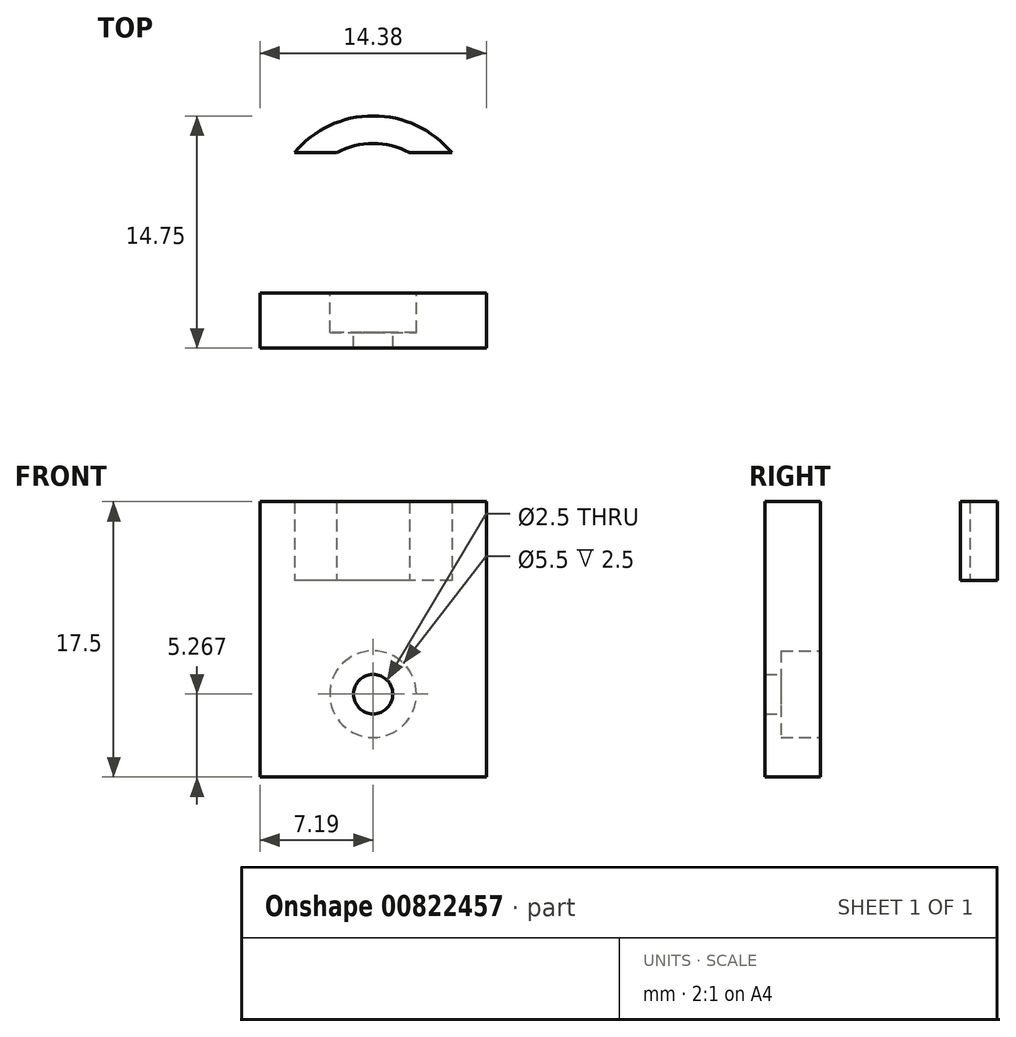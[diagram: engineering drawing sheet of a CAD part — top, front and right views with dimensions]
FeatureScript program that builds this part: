
annotation { "Feature Type Name" : "Feature", "Feature Type Description" : "" }
export const myFeature = defineFeature(function(context is Context, id is Id, definition is map)
    precondition{}
    {
        {
            var Q0;
            Q0=qCreatedBy(makeId("Top.planeOp"),FACE);
            var sketch = newSketch(context, id + "F0", { "sketchPlane" : qUnion([Q0])});
            skCircle(sketch, "E0", {"center": v(0, 0) * mm, "radius": 4.75 * mm});
            skCircle(sketch, "E1", {"center": v(0, 0) * mm, "radius": 6.5 * mm});
            skLineSegment(sketch, "E2", {"start": v(5, 4.15) * mm, "end": v(-5, 4.15) * mm});
            skLineSegment(sketch, "E3", {"start": v(0, -4.75) * mm, "end": v(-4.44, -4.75) * mm});
            skLineSegment(sketch, "E4", {"start": v(-4.44, -4.75) * mm, "end": v(-7.19, -4.75) * mm});
            skLineSegment(sketch, "E5", {"start": v(-7.19, -4.75) * mm, "end": v(-7.19, -8.25) * mm});
            skLineSegment(sketch, "E6", {"start": v(0, -4.75) * mm, "end": v(4.44, -4.75) * mm});
            skLineSegment(sketch, "E7", {"start": v(4.44, -4.75) * mm, "end": v(7.19, -4.75) * mm});
            skLineSegment(sketch, "E8", {"start": v(7.19, -4.75) * mm, "end": v(7.19, -8.25) * mm});
            skLineSegment(sketch, "E9", {"start": v(7.19, -8.25) * mm, "end": v(-7.19, -8.25) * mm});
            skSolve(sketch);
        }
        {
            var Q0;
            {var subQ0=sQuery(id+"F0.wireOp",EDGE,"E2");var subQ1=sQuery(id+"F0.wireOp",EDGE,"E0");var subQ2=makeQuery(id+"F0.imprint","INTERSECT",VERTEX,{"disambiguationData":[OD(0.0)],"derivedFrom":[subQ1,subQ0]});Q0=makeQuery(id+"F0.imprint","IMPRINT",FACE,{"disambiguationData":[TD([[makeQuery(id+"F0.imprint","IMPRINT",EDGE,{"disambiguationData":[TD([[subQ2,-1.0]])],"derivedFrom":subQ1}),-1.0]])]});}
            var Q1;
            {var subQ0=sQuery(id+"F0.wireOp",EDGE,"E2");var subQ1=sQuery(id+"F0.wireOp",EDGE,"E0");var subQ2=makeQuery(id+"F0.imprint","INTERSECT",VERTEX,{"disambiguationData":[OD(1.0)],"derivedFrom":[subQ1,subQ0]});Q1=makeQuery(id+"F0.imprint","IMPRINT",FACE,{"disambiguationData":[TD([[makeQuery(id+"F0.imprint","IMPRINT",EDGE,{"disambiguationData":[TD([[subQ2,1.0]])],"derivedFrom":subQ1}),-1.0]])]});}
            extrude(context, id + "F1", {"entities" : qUnion([Q0, Q1]), "endBound" : BoundingType.SYMMETRIC, "depth" : 5 * mm, "offsetDistance" : 25 * mm});
        }
        {
            var Q0;
            {var subQ1=sQuery(id+"F0.wireOp",EDGE,"E4");Q0=makeQuery(id+"F0.imprint","IMPRINT",FACE,{"disambiguationData":[TD([[makeQuery(id+"F0.imprint","IMPRINT",EDGE,{"derivedFrom":subQ1}),1.0]])]});}
            var Q1;
            {var subQ0=sQuery(id+"F0.wireOp",EDGE,"E3");Q1=makeQuery(id+"F0.imprint","IMPRINT",FACE,{"disambiguationData":[TD([[makeQuery(id+"F0.imprint","IMPRINT",EDGE,{"derivedFrom":subQ0}),1.0]])]});}
            extrude(context, id + "F2", {"entities" : qUnion([Q0, Q1]), "oppositeDirection" : true, "depth" : 15 * mm, "offsetDistance" : 25 * mm, "hasSecondDirection" : true, "secondDirectionOppositeDirection" : false, "secondDirectionDepth" : 2.5 * mm});
        }
        {
            var Q0;
            Q0=makeQuery(id+"F2.opExtrude","SWEPT_FACE",FACE,{"disambiguationData":[OSD([sQuery(id+"F0.wireOp",EDGE,"E3"),sQuery(id+"F0.wireOp",EDGE,"E4"),sQuery(id+"F0.wireOp",EDGE,"E6"),sQuery(id+"F0.wireOp",EDGE,"E7")])]});
            var sketch = newSketch(context, id + "F3", { "sketchPlane" : qUnion([Q0])});
            skCircle(sketch, "E10", {"center": v(0, -9.73) * mm, "radius": 1.25 * mm});
            skCircle(sketch, "E11", {"center": v(0, -9.73) * mm, "radius": 2.75 * mm});
            skSolve(sketch);
        }
        {
            var Q0;
            Q0=makeQuery(id+"F3.imprint","IMPRINT",FACE,{"disambiguationData":[TD([[makeQuery(id+"F3.imprint","IMPRINT",EDGE,{"derivedFrom":sQuery(id+"F3.wireOp",EDGE,"E10")}),1.0]])]});
            extrude(context, id + "F4", {"entities" : qUnion([Q0]), "operationType" : NewBodyOperationType.REMOVE, "oppositeDirection" : true, "depth" : 25 * mm, "offsetDistance" : 25 * mm});
        }
        {
            var Q0;
            Q0=makeQuery(id+"F3.imprint","IMPRINT",FACE,{"disambiguationData":[TD([[makeQuery(id+"F3.imprint","IMPRINT",EDGE,{"derivedFrom":sQuery(id+"F3.wireOp",EDGE,"E10")}),-1.0]])]});
            extrude(context, id + "F5", {"entities" : qUnion([Q0]), "operationType" : NewBodyOperationType.REMOVE, "oppositeDirection" : true, "depth" : 2.5 * mm, "offsetDistance" : 25 * mm});
        }
    });
